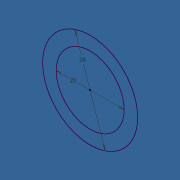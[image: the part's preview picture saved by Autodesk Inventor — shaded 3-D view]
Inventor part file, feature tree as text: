
AUTODESK INVENTOR PART (.ipt)
format: ipt  version: 2020 (Build 240168000, 168)  size: 82,944 bytes
history: native  units: mm
features: extrude x1, sketch x1
ambient origin geometry x8: Origin, YZ Plane, XZ Plane, XY Plane, X Axis, Y Axis, Z Axis, Center Point
bodies: Solid1 (feature_tree)
feature tree (2):
  extrude  "Extrusion1"  Depth=15.0mm
  sketch  "Sketch1"  dims[d0=28.0mm d1=21.0mm d2=84.5mm d3=15.0mm d4=0.0mm]
